# Revit family: FU_Chair_Sandler_CLASSY-1096M
name_source: partatom
category: Furniture
units: mm (PartAtom-declared; Revit-internal decimal feet)

## family parameters
Always vertical = No
Cut with Voids When Loaded = No
OmniClass Number = 23.21.23.15.17
Room Calculation Point = No
Shared = No
Work Plane-Based = Yes

## types (1)
- CLASSY 1096M
    BIMobject category = Chair
    BIMobject category code = furniture-chair
    BIMobject main category = Furniture
    BIMobject main category code = furniture
    Brand url = https://www.sandlerseating.com
    Default Elevation = 1219.2 mm  [stored 4 ft]
    Description = Chair
    Design country = UK
    Edition number = 1
    Frame = BS07 - CLASSY
    Frame Material = Wood - Ash - Black Stain
    Heigth Shell = 410 mm  [stored 1.34514 ft]
    IFC Classification = Furnishing Element
    Manufacturer = Sandler
    Manufacturer country = UK
    Manufacturer name = Sandler
    Masterformat 2014 Code = 12 48 43.13
    Masterformat 2014 Description = Chair Mats
    Model = CLASSY 1096M
    OmniClass Code = 23-21 23 15 17
    Product Guid = ??
    Product data url = https://www.sandlerseating.com
    Product family = Furniture
    Product group = Chair
    Product name = CLASSY 1096M
    Seat = TP02 - CLASSY
    Seat Material = Fabric - Gravity - Dove CPC17
    Shell Material = <By Category>
    Uniformat II Description = Movable Furnishings
    depth = 764.796 mm
    height = 761.804 mm
    width = 905.652 mm

note: [stored X ft] marks values corroborated as IEEE doubles in the binary element streams (Revit-internal decimal feet)

## geometry (parser evidence)
native form markers: Sweep x24
no freeform markers — native parametric forms only
